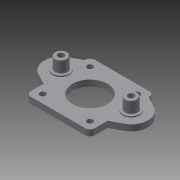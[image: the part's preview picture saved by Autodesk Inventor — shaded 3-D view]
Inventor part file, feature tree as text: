
AUTODESK INVENTOR PART (.ipt)
format: ipt  version: 2015 (Build 190159000, 159)  size: 195,072 bytes
history: native  units: mm
features: extrude x4, sketch x3, projected_geometry x3, chamfer x2, reference x2, fillet x1
ambient origin geometry x8: Origin, YZ Plane, XZ Plane, XY Plane, X Axis, Y Axis, Z Axis, Center Point
bodies: Solid1 (feature_tree)
feature tree (15):
  extrude  "Extrusion1"  Depth=3.75mm
  sketch  "Sketch2"  dims[d2=31.0mm d3=31.0mm]
  extrude  "Extrusion2"  Depth=31.0mm
  extrude  "Extrusion3"  Depth=42.0mm
  fillet  "Fillet1"  Radius=42.0mm
  extrude  "Extrusion4"  Depth=2.0mm
  chamfer  "Chamfer1"  Distance=4.0mm
  chamfer  "Chamfer2"  Distance=7.9mm
  sketch  "Sketch1"  dims[d0=23.0mm d1=3.75mm]
  reference  "Reference1"
  reference  "Reference2"
  projected_geometry  "Projected Loop1"
  sketch  "Sketch3"  dims[d4=22.0mm d5=42.0mm d6=42.0mm d7=23.0mm d8=4.0mm d9=7.9mm d10=3.0mm d11=8.0mm d12=11.0mm d13=4.0mm d14=0.0mm d15=11.0mm d16=7.9mm d17=7.9mm d18=11.0mm d19=8.5mm d20=0.0mm d21=0.75mm d22=0.0mm d23=0.5mm d24=4.0mm d25=8.0mm d26=0.0mm d27=0.25mm d28=2.0mm d29=45.0deg d30=0.25mm d31=2.0mm d32=45.0deg]
  projected_geometry  "Projected Loop2"
  projected_geometry  "Projected Loop3"
